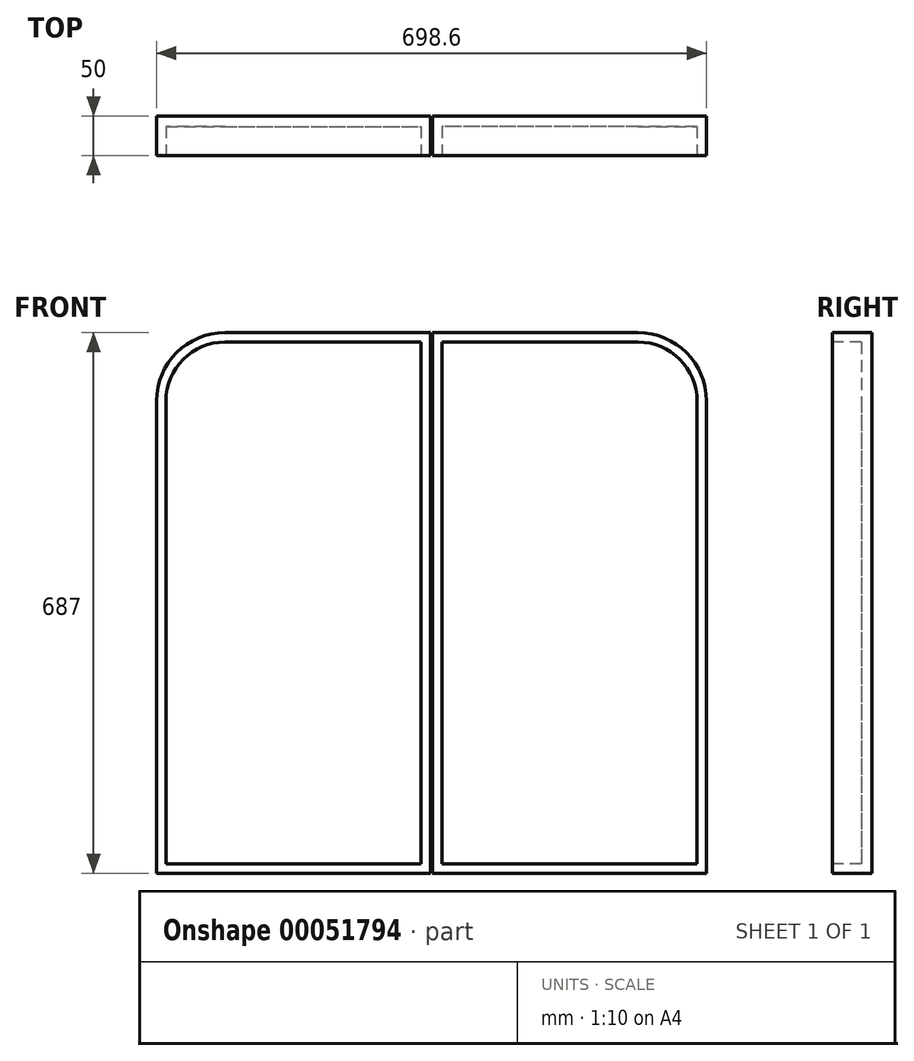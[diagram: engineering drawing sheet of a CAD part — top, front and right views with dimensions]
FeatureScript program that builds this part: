
annotation { "Feature Type Name" : "Feature", "Feature Type Description" : "" }
export const myFeature = defineFeature(function(context is Context, id is Id, definition is map)
    precondition{}
    {
        {
            var Q0;
            Q0=qCreatedBy(makeId("Front.planeOp"),FACE);
            var sketch = newSketch(context, id + "F0", { "sketchPlane" : qUnion([Q0])});
            skLineSegment(sketch, "E0.bottom", {"start": v(-262.3, 343.5) * mm, "end": v(-1.3, 343.5) * mm});
            skLineSegment(sketch, "E0.top", {"start": v(-349.3, -343.5) * mm, "end": v(-1.3, -343.5) * mm});
            skLineSegment(sketch, "E0.left", {"start": v(-349.3, 256.5) * mm, "end": v(-349.3, -343.5) * mm});
            skLineSegment(sketch, "E0.right", {"start": v(-1.3, 343.5) * mm, "end": v(-1.3, -343.5) * mm});
            skPoint(sketch, "E1.visualSharp", {"position": v(-349.3, 343.5) * mm});
            skArc(sketch, "E1.filletArc", {"start": v(-262.3, 343.5) * mm, "mid": v(-323.82, 318.02) * mm, "end": v(-349.3, 256.5) * mm});
            skSolve(sketch);
        }
        {
            var Q0;
            Q0=makeQuery(id+"F0.imprint","IMPRINT",FACE,{"disambiguationData":[TD([[makeQuery(id+"F0.imprint","IMPRINT",EDGE,{"derivedFrom":sQuery(id+"F0.wireOp",EDGE,"E0.bottom")}),-1.0]])]});
            extrude(context, id + "F1", {"entities" : qUnion([Q0]), "depth" : 50 * mm});
        }
        {
            var Q0;
            Q0=makeQuery(id+"F1.opExtrude","CAP_FACE",FACE,{"disambiguationData":[OSD([sQuery(id+"F0.wireOp",EDGE,"E0.bottom"),sQuery(id+"F0.wireOp",EDGE,"E0.top"),sQuery(id+"F0.wireOp",EDGE,"E0.left"),sQuery(id+"F0.wireOp",EDGE,"E0.right"),sQuery(id+"F0.wireOp",EDGE,"E1.filletArc")])],"isStart":false});
            var sketch = newSketch(context, id + "F2", { "sketchPlane" : qUnion([Q0])});
            skLineSegment(sketch, "E2.bottom", {"start": v(-262.3, 331.5) * mm, "end": v(-13.3, 331.5) * mm});
            skLineSegment(sketch, "E2.top", {"start": v(-337.3, -331.5) * mm, "end": v(-13.3, -331.5) * mm});
            skLineSegment(sketch, "E2.left", {"start": v(-337.3, 256.5) * mm, "end": v(-337.3, -331.5) * mm});
            skLineSegment(sketch, "E2.right", {"start": v(-13.3, 331.5) * mm, "end": v(-13.3, -331.5) * mm});
            skPoint(sketch, "E3.visualSharp", {"position": v(-337.3, 331.5) * mm});
            skArc(sketch, "E3.filletArc", {"start": v(-262.3, 331.5) * mm, "mid": v(-315.33, 309.53) * mm, "end": v(-337.3, 256.5) * mm});
            skSolve(sketch);
        }
        {
            var Q0;
            Q0=makeQuery(id+"F2.imprint","IMPRINT",FACE,{"disambiguationData":[TD([[makeQuery(id+"F2.imprint","IMPRINT",EDGE,{"derivedFrom":sQuery(id+"F2.wireOp",EDGE,"E2.bottom")}),-1.0]])]});
            extrude(context, id + "F3", {"entities" : qUnion([Q0]), "operationType" : NewBodyOperationType.REMOVE, "oppositeDirection" : true, "depth" : 37 * mm});
        }
        {
            var Q0;
            Q0=makeQuery(id+"F1.opExtrude","SWEPT_BODY",BODY,{"disambiguationData":[OSD([sQuery(id+"F0.wireOp",EDGE,"E0.bottom"),sQuery(id+"F0.wireOp",EDGE,"E0.top"),sQuery(id+"F0.wireOp",EDGE,"E0.left"),sQuery(id+"F0.wireOp",EDGE,"E0.right"),sQuery(id+"F0.wireOp",EDGE,"E1.filletArc")])]});
            var Q1;
            Q1=qCreatedBy(makeId("Right.planeOp"),FACE);
            mirror(context, id + "F4", {"entities" : qUnion([Q0]), "mirrorPlane" : qUnion([Q1])});
        }
    });
